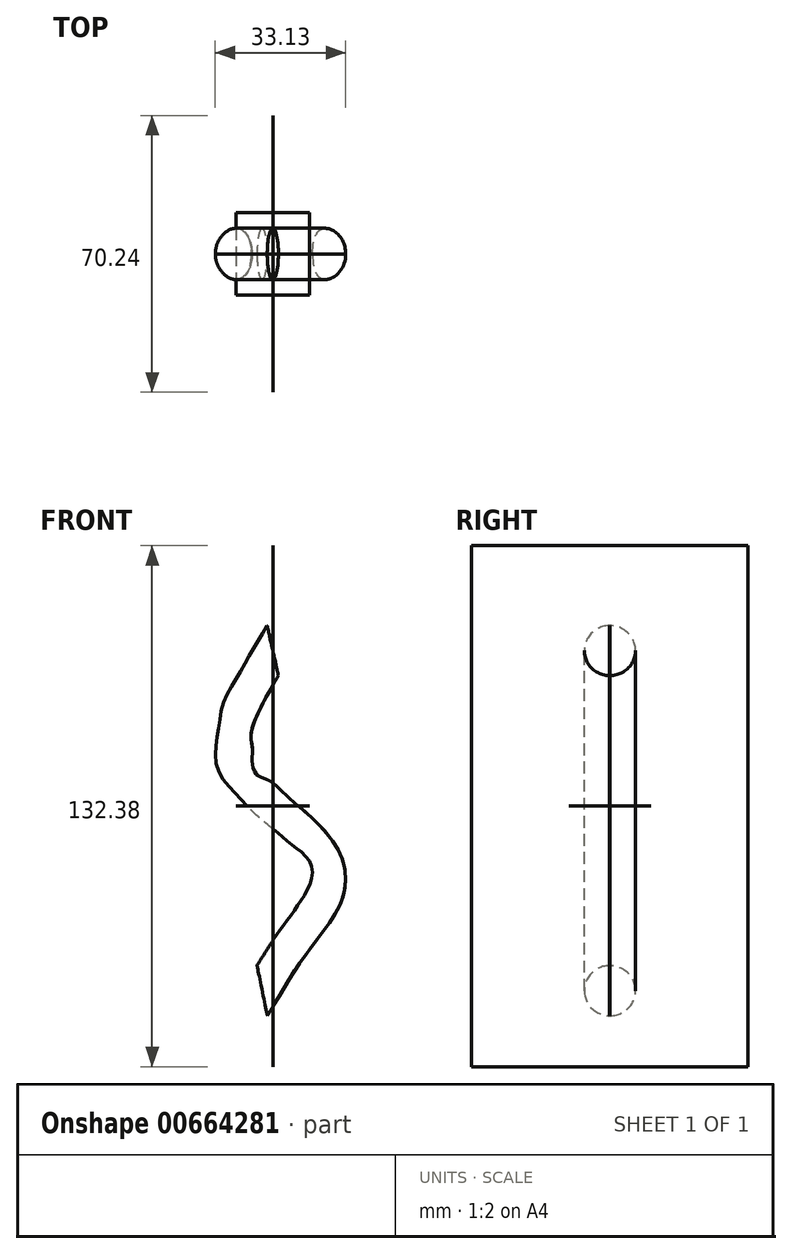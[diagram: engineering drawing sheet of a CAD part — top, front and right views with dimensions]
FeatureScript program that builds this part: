
annotation { "Feature Type Name" : "Feature", "Feature Type Description" : "" }
export const myFeature = defineFeature(function(context is Context, id is Id, definition is map)
    precondition{}
    {
        {
            var Q0;
            Q0=qCreatedBy(makeId("Front.planeOp"),FACE);
            var sketch = newSketch(context, id + "F0", { "sketchPlane" : qUnion([Q0])});
            skLineSegment(sketch, "E0.bottom", {"start": v(-47.26, 70.38) * mm, "end": v(47.26, 70.38) * mm});
            skLineSegment(sketch, "E0.top", {"start": v(-47.26, -70.38) * mm, "end": v(47.26, -70.38) * mm});
            skLineSegment(sketch, "E0.left", {"start": v(-47.26, 70.38) * mm, "end": v(-47.26, -70.38) * mm});
            skLineSegment(sketch, "E0.right", {"start": v(47.26, 70.38) * mm, "end": v(47.26, -70.38) * mm});
            skPoint(sketch, "E0.middle", {"position": v(0, 0) * mm});
            skSolve(sketch);
        }
        {
            var Q0;
            Q0 = qSketchRegion(id + "F0", true);
            extrude(context, id + "F1", {"entities" : qUnion([Q0]), "depth" : 0.1 * mm, "offsetDistance" : 25 * mm});
        }
        {
            var Q0;
            Q0=qCreatedBy(makeId("Top.planeOp"),FACE);
            var sketch = newSketch(context, id + "F2", { "sketchPlane" : qUnion([Q0])});
            skLineSegment(sketch, "E1.bottom", {"start": v(9.39, 10.44) * mm, "end": v(-9.39, 10.44) * mm});
            skLineSegment(sketch, "E1.top", {"start": v(9.39, -10.44) * mm, "end": v(-9.39, -10.44) * mm});
            skLineSegment(sketch, "E1.left", {"start": v(9.39, 10.44) * mm, "end": v(9.39, -10.44) * mm});
            skLineSegment(sketch, "E1.right", {"start": v(-9.39, 10.44) * mm, "end": v(-9.39, -10.44) * mm});
            skPoint(sketch, "E1.middle", {"position": v(0, 0) * mm});
            skSolve(sketch);
        }
        {
            var Q0;
            Q0 = qSketchRegion(id + "F2", true);
            extrude(context, id + "F3", {"entities" : qUnion([Q0]), "depth" : 0.1 * mm, "offsetDistance" : 25 * mm});
        }
        {
            var Q0;
            Q0=qCreatedBy(makeId("Right.planeOp"),FACE);
            var sketch = newSketch(context, id + "F4", { "sketchPlane" : qUnion([Q0])});
            skLineSegment(sketch, "E2.bottom", {"start": v(35.12, 66.2) * mm, "end": v(-35.12, 66.2) * mm});
            skLineSegment(sketch, "E2.top", {"start": v(35.12, -66.2) * mm, "end": v(-35.12, -66.2) * mm});
            skLineSegment(sketch, "E2.left", {"start": v(35.12, 66.2) * mm, "end": v(35.12, -66.2) * mm});
            skLineSegment(sketch, "E2.right", {"start": v(-35.12, 66.2) * mm, "end": v(-35.12, -66.2) * mm});
            skPoint(sketch, "E2.middle", {"position": v(0, 0) * mm});
            skSolve(sketch);
        }
        {
            var Q0;
            Q0 = qSketchRegion(id + "F4", true);
            extrude(context, id + "F5", {"entities" : qUnion([Q0]), "depth" : 0.1 * mm, "offsetDistance" : 25 * mm});
        }
        {
            var Q0;
            Q0=qCreatedBy(makeId("Front.planeOp"),FACE);
            var sketch = newSketch(context, id + "F6", { "sketchPlane" : qUnion([Q0])});
            skFitSpline(sketch, "E3", {"points": [v(0, 39.52) * mm, v(-8.07, 24.22) * mm, v(-9.2, 18.27) * mm, v(-8.92, 10.62) * mm, v(-4.96, 4.96) * mm, v(0, 0) * mm, v(6.37, -5.8) * mm, v(12.32, -13.46) * mm, v(13.17, -20.54) * mm, v(9.77, -27.9) * mm, v(3.54, -36.97) * mm, v(-2.7, -46.88) * mm], "startDerivative": vector(-79.55, -136.33) * mm, "endDerivative": vector(-58.56, -96.56) * mm});
            skSolve(sketch);
        }
        {
            var Q0;
            Q0=qCreatedBy(makeId("Top.planeOp"),FACE);
            var sketch = newSketch(context, id + "F7", { "sketchPlane" : qUnion([Q0])});
            skCircle(sketch, "E4", {"center": v(0, 0) * mm, "radius": 6.5 * mm});
            skSolve(sketch);
        }
        {
            var Q0;
            Q0=makeQuery(id+"F7.imprint","IMPRINT",FACE,{"disambiguationData":[TD([[makeQuery(id+"F7.imprint","IMPRINT",EDGE,{"derivedFrom":sQuery(id+"F7.wireOp",EDGE,"E4")}),1.0]])]});
            var Q1;
            Q1=sQuery(id+"F6.wireOp",EDGE,"E3");
            sweep(context, id + "F8", {"profiles" : qUnion([Q0]), "path" : qUnion([Q1])});
        }
        {
            var Q0;
            Q0=makeQuery(id+"F1.opExtrude","SWEPT_BODY",BODY,{"disambiguationData":[OSD([sQuery(id+"F0.wireOp",EDGE,"E0.bottom"),sQuery(id+"F0.wireOp",EDGE,"E0.top"),sQuery(id+"F0.wireOp",EDGE,"E0.left"),sQuery(id+"F0.wireOp",EDGE,"E0.right")])]});
            var Q1;
            Q1=makeQuery(id+"F8.opSweep","SWEPT_BODY",BODY,{"disambiguationData":[OSD([sQuery(id+"F6.wireOp",EDGE,"E3"),sQuery(id+"F7.wireOp",EDGE,"E4")])]});
            booleanBodies(context, id + "F9", {"operationType" : BooleanOperationType.SUBTRACTION, "tools" : qUnion([Q0]), "targets" : qUnion([Q1])});
        }
        {
            var Q0;
            Q0=makeQuery(id+"F9.opBoolean","SPLIT",BODY,{"disambiguationData":[OD(4.0)],"derivedFrom":makeQuery(id+"F8.opSweep","SWEPT_BODY",BODY,{"disambiguationData":[OSD([sQuery(id+"F6.wireOp",EDGE,"E3"),sQuery(id+"F7.wireOp",EDGE,"E4")])]})});
            transform(context, id + "F10", {"entities" : qUnion([Q0]), "transformType" : TransformType.TRANSLATION_3D, "dx" : 0 * mm, "dy" : 10 * mm, "dz" : 0 * mm, "makeCopy" : false});
        }
        {
            var Q0;
            Q0=makeQuery(id+"F9.opBoolean","SPLIT",BODY,{"disambiguationData":[OD(5.0)],"derivedFrom":makeQuery(id+"F8.opSweep","SWEPT_BODY",BODY,{"disambiguationData":[OSD([sQuery(id+"F6.wireOp",EDGE,"E3"),sQuery(id+"F7.wireOp",EDGE,"E4")])]})});
            transform(context, id + "F11", {"entities" : qUnion([Q0]), "transformType" : TransformType.TRANSLATION_3D, "dx" : 0 * mm, "dy" : -10 * mm, "dz" : 0 * mm, "makeCopy" : false});
        }
        {
            var Q0;
            Q0=makeQuery(id+"F9.opBoolean","SPLIT",BODY,{"disambiguationData":[OD(7.0)],"derivedFrom":makeQuery(id+"F8.opSweep","SWEPT_BODY",BODY,{"disambiguationData":[OSD([sQuery(id+"F6.wireOp",EDGE,"E3"),sQuery(id+"F7.wireOp",EDGE,"E4")])]})});
            transform(context, id + "F12", {"entities" : qUnion([Q0]), "transformType" : TransformType.TRANSLATION_3D, "dx" : 0 * mm, "dy" : -10 * mm, "dz" : 0 * mm, "makeCopy" : false});
        }
        {
            var Q0;
            Q0=makeQuery(id+"F9.opBoolean","SPLIT",BODY,{"disambiguationData":[OD(6.0)],"derivedFrom":makeQuery(id+"F8.opSweep","SWEPT_BODY",BODY,{"disambiguationData":[OSD([sQuery(id+"F6.wireOp",EDGE,"E3"),sQuery(id+"F7.wireOp",EDGE,"E4")])]})});
            transform(context, id + "F13", {"entities" : qUnion([Q0]), "transformType" : TransformType.TRANSLATION_3D, "dx" : 0 * mm, "dy" : 10 * mm, "dz" : 0 * mm, "makeCopy" : false});
        }
    });
